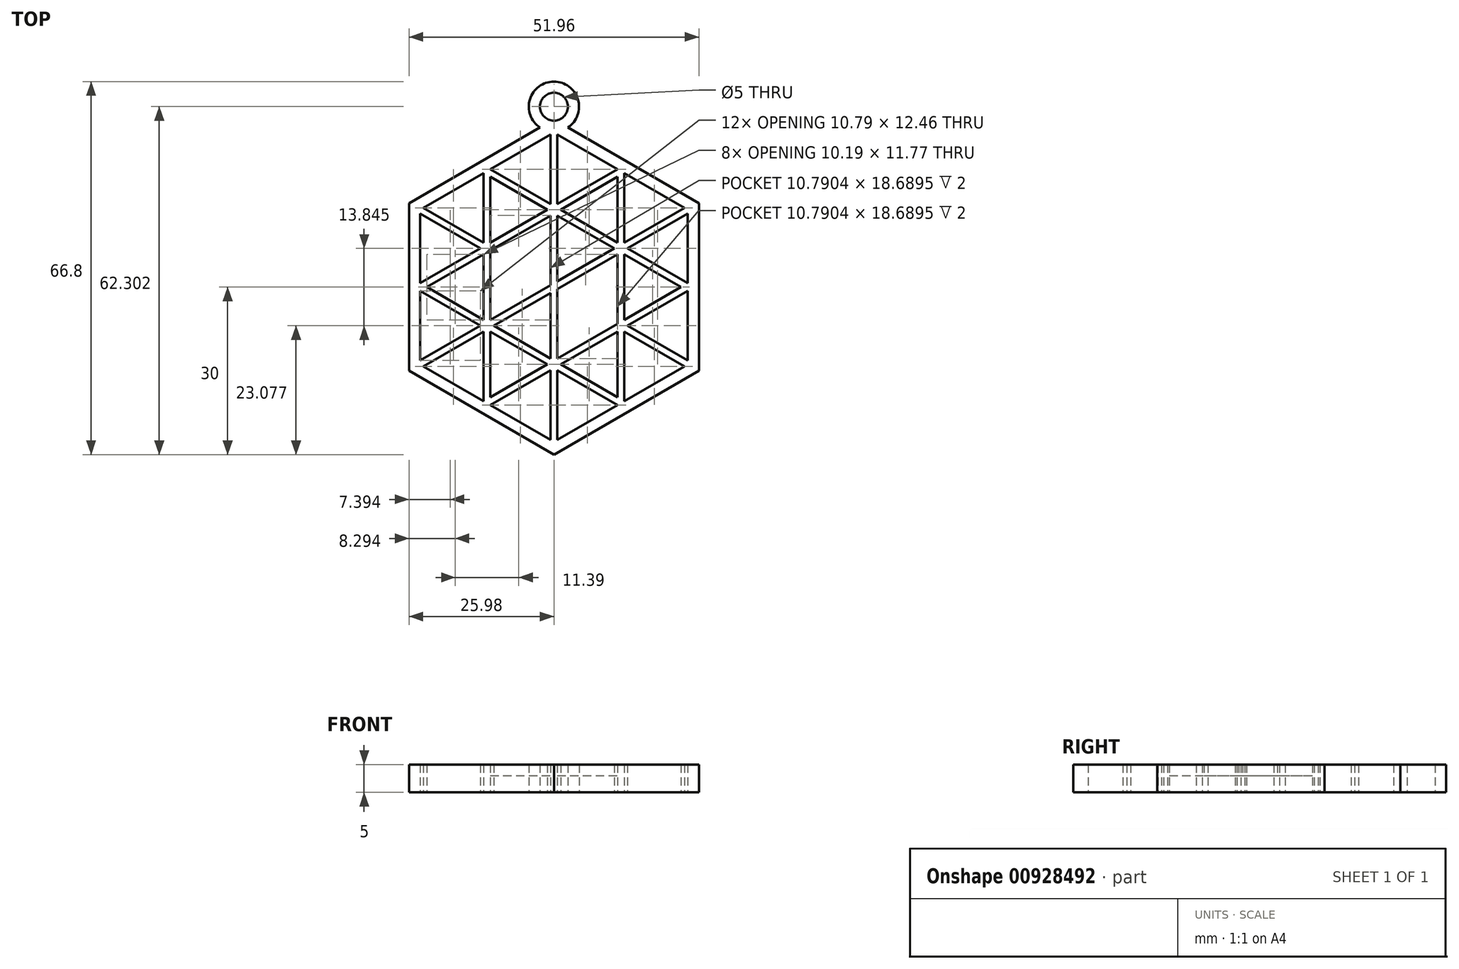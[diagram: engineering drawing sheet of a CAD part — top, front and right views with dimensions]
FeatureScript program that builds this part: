
annotation { "Feature Type Name" : "Feature", "Feature Type Description" : "" }
export const myFeature = defineFeature(function(context is Context, id is Id, definition is map)
    precondition{}
    {
        {
            var Q0;
            Q0=qCreatedBy(makeId("Top.planeOp"),FACE);
            var sketch = newSketch(context, id + "F0", { "sketchPlane" : qUnion([Q0])});
            skLineSegment(sketch, "E0.0", {"start": v(2.5, 28.56) * mm, "end": v(25.98, 15) * mm});
            skLineSegment(sketch, "E0.1", {"start": v(25.98, 15) * mm, "end": v(25.98, -15) * mm});
            skLineSegment(sketch, "E0.2", {"start": v(25.98, -15) * mm, "end": v(0, -30) * mm});
            skLineSegment(sketch, "E0.3", {"start": v(0, -30) * mm, "end": v(-25.98, -15) * mm});
            skLineSegment(sketch, "E0.4", {"start": v(-25.98, -15) * mm, "end": v(-25.98, 15) * mm});
            skLineSegment(sketch, "E0.5", {"start": v(-25.98, 15) * mm, "end": v(-2.5, 28.56) * mm});
            skLineSegment(sketch, "E1.0", {"start": v(0.6, 27.34) * mm, "end": v(23.38, 14.2) * mm});
            skLineSegment(sketch, "E1.1", {"start": v(23.98, 13.15) * mm, "end": v(23.98, 0.7) * mm});
            skLineSegment(sketch, "E1.2", {"start": v(23.38, -14.2) * mm, "end": v(12.6, -20.42) * mm});
            skLineSegment(sketch, "E1.3", {"start": v(-0.6, -27.34) * mm, "end": v(-11.4, -21.11) * mm});
            skLineSegment(sketch, "E1.4", {"start": v(-23.98, -13.15) * mm, "end": v(-23.98, -0.7) * mm});
            skLineSegment(sketch, "E1.5", {"start": v(-23.38, 14.2) * mm, "end": v(-12.6, 20.42) * mm});
            skLineSegment(sketch, "E2", {"start": v(-23.98, -13.85) * mm, "end": v(23.98, 13.85) * mm, "construction": true});
            skLineSegment(sketch, "E3", {"start": v(-23.98, 0) * mm, "end": v(12, 20.77) * mm, "construction": true});
            skLineSegment(sketch, "E4", {"start": v(-12, -20.77) * mm, "end": v(23.98, 0) * mm, "construction": true});
            skLineSegment(sketch, "E5", {"start": v(0, -27.7) * mm, "end": v(0, 27.7) * mm, "construction": true});
            skLineSegment(sketch, "E6", {"start": v(-12, -20.77) * mm, "end": v(-12, 20.77) * mm, "construction": true});
            skLineSegment(sketch, "E7", {"start": v(12, -20.77) * mm, "end": v(12, 20.77) * mm, "construction": true});
            skLineSegment(sketch, "E8", {"start": v(23.98, -13.85) * mm, "end": v(-23.98, 13.85) * mm, "construction": true});
            skLineSegment(sketch, "E9", {"start": v(12, -20.77) * mm, "end": v(-23.98, 0) * mm, "construction": true});
            skLineSegment(sketch, "E10", {"start": v(23.98, 0) * mm, "end": v(-12, 20.77) * mm, "construction": true});
            skLineSegment(sketch, "E11.0", {"start": v(12.6, -20.42) * mm, "end": v(12.6, -7.96) * mm});
            skLineSegment(sketch, "E12.0", {"start": v(0.6, -27.7) * mm, "end": v(0.6, -27.68) * mm});
            skLineSegment(sketch, "E13.0", {"start": v(-0.6, -27.7) * mm, "end": v(-0.6, -27.68) * mm});
            skLineSegment(sketch, "E14.0", {"start": v(-12.6, -20.42) * mm, "end": v(-12.6, -7.96) * mm});
            skLineSegment(sketch, "E15.0", {"start": v(-11.4, -21.11) * mm, "end": v(-0.6, -14.88) * mm});
            skLineSegment(sketch, "E16.0", {"start": v(-23.68, -14.36) * mm, "end": v(-23.68, -14.36) * mm});
            skLineSegment(sketch, "E17.0", {"start": v(-22.78, 0) * mm, "end": v(-12.6, 5.88) * mm});
            skLineSegment(sketch, "E18.0", {"start": v(-23.98, 0.7) * mm, "end": v(-13.2, 6.92) * mm});
            skLineSegment(sketch, "E19.0", {"start": v(-24.28, -13.33) * mm, "end": v(-24.28, -13.32) * mm});
            skLineSegment(sketch, "E20.0", {"start": v(-11.4, -19.73) * mm, "end": v(-1.2, -13.85) * mm});
            skLineSegment(sketch, "E21.0", {"start": v(23.98, 0.7) * mm, "end": v(13.2, 6.92) * mm});
            skLineSegment(sketch, "E22.0", {"start": v(24.28, -13.33) * mm, "end": v(24.28, -13.32) * mm});
            skLineSegment(sketch, "E23.0", {"start": v(23.68, -14.36) * mm, "end": v(23.68, -14.36) * mm});
            skLineSegment(sketch, "E24.0", {"start": v(11.4, -21.11) * mm, "end": v(0.6, -14.88) * mm});
            skLineSegment(sketch, "E25.trimOffspring", {"start": v(23.68, 14.36) * mm, "end": v(23.68, 14.36) * mm});
            skLineSegment(sketch, "E26.trimOffspring", {"start": v(24.28, 13.32) * mm, "end": v(24.28, 13.33) * mm});
            skLineSegment(sketch, "E27.trimOffspring", {"start": v(23.98, -0.7) * mm, "end": v(23.98, -13.15) * mm});
            skLineSegment(sketch, "E28.trimOffspring", {"start": v(22.78, 0) * mm, "end": v(12.6, 5.88) * mm});
            skLineSegment(sketch, "E29.trimOffspring", {"start": v(23.38, -14.2) * mm, "end": v(12.6, -7.96) * mm});
            skLineSegment(sketch, "E30.trimOffspring", {"start": v(23.98, -13.15) * mm, "end": v(13.2, -6.92) * mm});
            skLineSegment(sketch, "E31.trimOffspring", {"start": v(11.4, -21.11) * mm, "end": v(0.6, -27.34) * mm});
            skLineSegment(sketch, "E32.trimOffspring", {"start": v(11.4, -19.73) * mm, "end": v(11.4, -7.96) * mm});
            skLineSegment(sketch, "E33.trimOffspring", {"start": v(11.4, -19.73) * mm, "end": v(1.2, -13.85) * mm});
            skLineSegment(sketch, "E34.trimOffspring", {"start": v(0.6, -27.34) * mm, "end": v(0.6, -14.88) * mm});
            skLineSegment(sketch, "E35.trimOffspring", {"start": v(-0.6, -27.34) * mm, "end": v(-0.6, -14.88) * mm});
            skLineSegment(sketch, "E36.trimOffspring", {"start": v(-12.6, -20.42) * mm, "end": v(-23.38, -14.2) * mm});
            skLineSegment(sketch, "E37.trimOffspring", {"start": v(-11.4, -19.73) * mm, "end": v(-11.4, -7.96) * mm});
            skLineSegment(sketch, "E38.trimOffspring", {"start": v(-23.98, -13.15) * mm, "end": v(-13.2, -6.92) * mm});
            skLineSegment(sketch, "E39.trimOffspring", {"start": v(-23.38, -14.2) * mm, "end": v(-12.6, -7.96) * mm});
            skLineSegment(sketch, "E40.trimOffspring", {"start": v(-23.98, 0.7) * mm, "end": v(-23.98, 13.15) * mm});
            skLineSegment(sketch, "E41.trimOffspring", {"start": v(-23.68, 14.36) * mm, "end": v(-23.68, 14.36) * mm});
            skLineSegment(sketch, "E42.trimOffspring", {"start": v(-24.28, 13.32) * mm, "end": v(-24.28, 13.33) * mm});
            skLineSegment(sketch, "E43.trimOffspring", {"start": v(-11.4, 21.11) * mm, "end": v(-0.6, 27.34) * mm});
            skLineSegment(sketch, "E44.trimOffspring", {"start": v(-0.6, 27.68) * mm, "end": v(-0.6, 27.7) * mm});
            skLineSegment(sketch, "E45.trimOffspring", {"start": v(0.6, 27.68) * mm, "end": v(0.6, 27.7) * mm});
            skLineSegment(sketch, "E46.trimOffspring", {"start": v(12.6, 7.96) * mm, "end": v(12.6, 20.42) * mm});
            skLineSegment(sketch, "E47.trimOffspring", {"start": v(13.2, 6.92) * mm, "end": v(23.98, 13.15) * mm});
            skLineSegment(sketch, "E48.trimOffspring", {"start": v(10.8, 6.92) * mm, "end": v(0.6, 12.8) * mm});
            skLineSegment(sketch, "E49.trimOffspring", {"start": v(11.4, 7.96) * mm, "end": v(11.4, 19.73) * mm});
            skLineSegment(sketch, "E50.trimOffspring", {"start": v(12.6, 7.96) * mm, "end": v(23.38, 14.2) * mm});
            skLineSegment(sketch, "E51.trimOffspring", {"start": v(11.4, 7.96) * mm, "end": v(1.2, 13.85) * mm});
            skLineSegment(sketch, "E52.trimOffspring", {"start": v(1.2, 13.85) * mm, "end": v(11.4, 19.73) * mm});
            skLineSegment(sketch, "E53.trimOffspring", {"start": v(-0.6, 14.88) * mm, "end": v(-11.4, 21.11) * mm});
            skLineSegment(sketch, "E54.trimOffspring", {"start": v(0.6, 14.88) * mm, "end": v(11.4, 21.11) * mm});
            skLineSegment(sketch, "E55.trimOffspring", {"start": v(-1.2, 13.85) * mm, "end": v(-11.4, 19.73) * mm});
            skLineSegment(sketch, "E56.trimOffspring", {"start": v(-0.6, 14.88) * mm, "end": v(-0.6, 27.34) * mm});
            skLineSegment(sketch, "E57.trimOffspring", {"start": v(0.6, 14.88) * mm, "end": v(0.6, 27.34) * mm});
            skLineSegment(sketch, "E58.trimOffspring", {"start": v(-13.2, 6.92) * mm, "end": v(-23.98, 13.15) * mm});
            skLineSegment(sketch, "E59.trimOffspring", {"start": v(-12.6, 7.96) * mm, "end": v(-23.38, 14.2) * mm});
            skLineSegment(sketch, "E60.trimOffspring", {"start": v(0.6, 1.04) * mm, "end": v(0.6, 12.8) * mm});
            skLineSegment(sketch, "E61.trimOffspring", {"start": v(0.6, 1.04) * mm, "end": v(10.8, 6.92) * mm});
            skLineSegment(sketch, "E62.trimOffspring", {"start": v(-0.6, 0.35) * mm, "end": v(-0.6, 12.8) * mm});
            skLineSegment(sketch, "E63.trimOffspring", {"start": v(0.6, -0.35) * mm, "end": v(11.4, 5.88) * mm});
            skLineSegment(sketch, "E64.trimOffspring", {"start": v(12.6, -5.88) * mm, "end": v(22.78, 0) * mm});
            skLineSegment(sketch, "E65.trimOffspring", {"start": v(12.6, -5.88) * mm, "end": v(12.6, 5.88) * mm});
            skLineSegment(sketch, "E66.trimOffspring", {"start": v(13.2, -6.92) * mm, "end": v(23.98, -0.7) * mm});
            skLineSegment(sketch, "E67.trimOffspring", {"start": v(11.4, -6.58) * mm, "end": v(11.4, 5.88) * mm});
            skLineSegment(sketch, "E68.trimOffspring", {"start": v(0.6, -12.8) * mm, "end": v(11.4, -6.58) * mm});
            skLineSegment(sketch, "E69.trimOffspring", {"start": v(-0.6, -12.8) * mm, "end": v(-10.8, -6.92) * mm});
            skLineSegment(sketch, "E70.trimOffspring", {"start": v(0.6, -12.8) * mm, "end": v(0.6, -0.35) * mm});
            skLineSegment(sketch, "E71.trimOffspring", {"start": v(1.2, -13.85) * mm, "end": v(11.4, -7.96) * mm});
            skLineSegment(sketch, "E72.trimOffspring", {"start": v(-0.6, -12.8) * mm, "end": v(-0.6, -1.04) * mm});
            skLineSegment(sketch, "E73.trimOffspring", {"start": v(-1.2, -13.85) * mm, "end": v(-11.4, -7.96) * mm});
            skLineSegment(sketch, "E74.trimOffspring", {"start": v(-12.6, -5.88) * mm, "end": v(-22.78, 0) * mm});
            skLineSegment(sketch, "E75.trimOffspring", {"start": v(-12.6, -5.88) * mm, "end": v(-12.6, 5.88) * mm});
            skLineSegment(sketch, "E76.trimOffspring", {"start": v(-11.4, -5.88) * mm, "end": v(-0.6, 0.35) * mm});
            skLineSegment(sketch, "E77.trimOffspring", {"start": v(-11.4, -5.88) * mm, "end": v(-11.4, 6.58) * mm});
            skLineSegment(sketch, "E78.trimOffspring", {"start": v(-10.8, -6.92) * mm, "end": v(-0.6, -1.04) * mm});
            skLineSegment(sketch, "E79.trimOffspring", {"start": v(-13.2, -6.92) * mm, "end": v(-23.98, -0.7) * mm});
            skLineSegment(sketch, "E80.trimOffspring", {"start": v(-11.4, 6.58) * mm, "end": v(-0.6, 12.8) * mm});
            skLineSegment(sketch, "E81.trimOffspring", {"start": v(-11.4, 7.96) * mm, "end": v(-11.4, 19.73) * mm});
            skLineSegment(sketch, "E82.trimOffspring", {"start": v(-11.4, 7.96) * mm, "end": v(-1.2, 13.85) * mm});
            skLineSegment(sketch, "E83.trimOffspring", {"start": v(-12.6, 7.96) * mm, "end": v(-12.6, 20.42) * mm});
            skArc(sketch, "E84", {"start": v(2.5, 28.56) * mm, "mid": v(0, 36.8) * mm, "end": v(-2.5, 28.56) * mm});
            skCircle(sketch, "E85", {"center": v(0, 32.3) * mm, "radius": 2.5 * mm});
            skPoint(sketch, "E86.orphan", {"position": v(0, 30) * mm});
            skSolve(sketch);
        }
        {
            var Q0;
            Q0=qSketchRegion(id+"F0",true);
            extrude(context, id + "F1", {"entities" : qUnion([Q0]), "depth" : 5 * mm, "offsetDistance" : 25 * mm});
        }
        {
            var Q0;
            Q0=makeQuery(id+"F1.opExtrude","CAP_FACE",FACE,{"disambiguationData":[OSD([sQuery(id+"F0.wireOp",EDGE,"E0.0"),sQuery(id+"F0.wireOp",EDGE,"E0.1"),sQuery(id+"F0.wireOp",EDGE,"E0.2"),sQuery(id+"F0.wireOp",EDGE,"E0.3"),sQuery(id+"F0.wireOp",EDGE,"E0.4"),sQuery(id+"F0.wireOp",EDGE,"E0.5"),sQuery(id+"F0.wireOp",EDGE,"E1.0"),sQuery(id+"F0.wireOp",EDGE,"E1.1"),sQuery(id+"F0.wireOp",EDGE,"E1.2"),sQuery(id+"F0.wireOp",EDGE,"E1.3"),sQuery(id+"F0.wireOp",EDGE,"E1.4"),sQuery(id+"F0.wireOp",EDGE,"E1.5"),sQuery(id+"F0.wireOp",EDGE,"E11.0"),sQuery(id+"F0.wireOp",EDGE,"E14.0"),sQuery(id+"F0.wireOp",EDGE,"E15.0"),sQuery(id+"F0.wireOp",EDGE,"E17.0"),sQuery(id+"F0.wireOp",EDGE,"E18.0"),sQuery(id+"F0.wireOp",EDGE,"E20.0"),sQuery(id+"F0.wireOp",EDGE,"E21.0"),sQuery(id+"F0.wireOp",EDGE,"E24.0"),sQuery(id+"F0.wireOp",EDGE,"E27.trimOffspring"),sQuery(id+"F0.wireOp",EDGE,"E28.trimOffspring"),sQuery(id+"F0.wireOp",EDGE,"E29.trimOffspring"),sQuery(id+"F0.wireOp",EDGE,"E30.trimOffspring"),sQuery(id+"F0.wireOp",EDGE,"E31.trimOffspring"),sQuery(id+"F0.wireOp",EDGE,"E32.trimOffspring"),sQuery(id+"F0.wireOp",EDGE,"E33.trimOffspring"),sQuery(id+"F0.wireOp",EDGE,"E34.trimOffspring"),sQuery(id+"F0.wireOp",EDGE,"E35.trimOffspring"),sQuery(id+"F0.wireOp",EDGE,"E36.trimOffspring"),sQuery(id+"F0.wireOp",EDGE,"E37.trimOffspring"),sQuery(id+"F0.wireOp",EDGE,"E38.trimOffspring"),sQuery(id+"F0.wireOp",EDGE,"E39.trimOffspring"),sQuery(id+"F0.wireOp",EDGE,"E40.trimOffspring"),sQuery(id+"F0.wireOp",EDGE,"E43.trimOffspring"),sQuery(id+"F0.wireOp",EDGE,"E46.trimOffspring"),sQuery(id+"F0.wireOp",EDGE,"E47.trimOffspring"),sQuery(id+"F0.wireOp",EDGE,"E48.trimOffspring"),sQuery(id+"F0.wireOp",EDGE,"E49.trimOffspring"),sQuery(id+"F0.wireOp",EDGE,"E50.trimOffspring"),sQuery(id+"F0.wireOp",EDGE,"E51.trimOffspring"),sQuery(id+"F0.wireOp",EDGE,"E52.trimOffspring"),sQuery(id+"F0.wireOp",EDGE,"E53.trimOffspring"),sQuery(id+"F0.wireOp",EDGE,"E54.trimOffspring"),sQuery(id+"F0.wireOp",EDGE,"E55.trimOffspring"),sQuery(id+"F0.wireOp",EDGE,"E56.trimOffspring"),sQuery(id+"F0.wireOp",EDGE,"E57.trimOffspring"),sQuery(id+"F0.wireOp",EDGE,"E58.trimOffspring"),sQuery(id+"F0.wireOp",EDGE,"E59.trimOffspring"),sQuery(id+"F0.wireOp",EDGE,"E60.trimOffspring"),sQuery(id+"F0.wireOp",EDGE,"E61.trimOffspring"),sQuery(id+"F0.wireOp",EDGE,"E62.trimOffspring"),sQuery(id+"F0.wireOp",EDGE,"E63.trimOffspring"),sQuery(id+"F0.wireOp",EDGE,"E64.trimOffspring"),sQuery(id+"F0.wireOp",EDGE,"E65.trimOffspring"),sQuery(id+"F0.wireOp",EDGE,"E66.trimOffspring"),sQuery(id+"F0.wireOp",EDGE,"E67.trimOffspring"),sQuery(id+"F0.wireOp",EDGE,"E68.trimOffspring"),sQuery(id+"F0.wireOp",EDGE,"E69.trimOffspring"),sQuery(id+"F0.wireOp",EDGE,"E70.trimOffspring"),sQuery(id+"F0.wireOp",EDGE,"E71.trimOffspring"),sQuery(id+"F0.wireOp",EDGE,"E72.trimOffspring"),sQuery(id+"F0.wireOp",EDGE,"E73.trimOffspring"),sQuery(id+"F0.wireOp",EDGE,"E74.trimOffspring"),sQuery(id+"F0.wireOp",EDGE,"E75.trimOffspring"),sQuery(id+"F0.wireOp",EDGE,"E76.trimOffspring"),sQuery(id+"F0.wireOp",EDGE,"E77.trimOffspring"),sQuery(id+"F0.wireOp",EDGE,"E78.trimOffspring"),sQuery(id+"F0.wireOp",EDGE,"E79.trimOffspring"),sQuery(id+"F0.wireOp",EDGE,"E80.trimOffspring"),sQuery(id+"F0.wireOp",EDGE,"E81.trimOffspring"),sQuery(id+"F0.wireOp",EDGE,"E82.trimOffspring"),sQuery(id+"F0.wireOp",EDGE,"E83.trimOffspring")])],"isStart":true});
            var sketch = newSketch(context, id + "F2", { "sketchPlane" : qUnion([Q0])});
            skLineSegment(sketch, "E87", {"start": v(-0.6, -12.8) * mm, "end": v(-0.6, -0.35) * mm});
            skLineSegment(sketch, "E88", {"start": v(-0.6, -0.35) * mm, "end": v(-11.4, 5.88) * mm});
            skLineSegment(sketch, "E89", {"start": v(-11.4, 5.88) * mm, "end": v(-11.4, -6.58) * mm});
            skLineSegment(sketch, "E90", {"start": v(-11.4, -6.58) * mm, "end": v(-0.6, -12.8) * mm});
            skLineSegment(sketch, "E91", {"start": v(11.4, -5.88) * mm, "end": v(11.4, 6.58) * mm});
            skLineSegment(sketch, "E92", {"start": v(11.4, 6.58) * mm, "end": v(0.6, 12.8) * mm});
            skLineSegment(sketch, "E93", {"start": v(0.6, 12.8) * mm, "end": v(0.6, 0.35) * mm});
            skLineSegment(sketch, "E94", {"start": v(0.6, 0.35) * mm, "end": v(11.4, -5.88) * mm});
            skSolve(sketch);
        }
        {
            var Q0;
            Q0=qSketchRegion(id+"F2",true);
            extrude(context, id + "F3", {"entities" : qUnion([Q0]), "operationType" : NewBodyOperationType.ADD, "oppositeDirection" : true, "depth" : 3 * mm, "offsetDistance" : 25 * mm});
        }
    });
